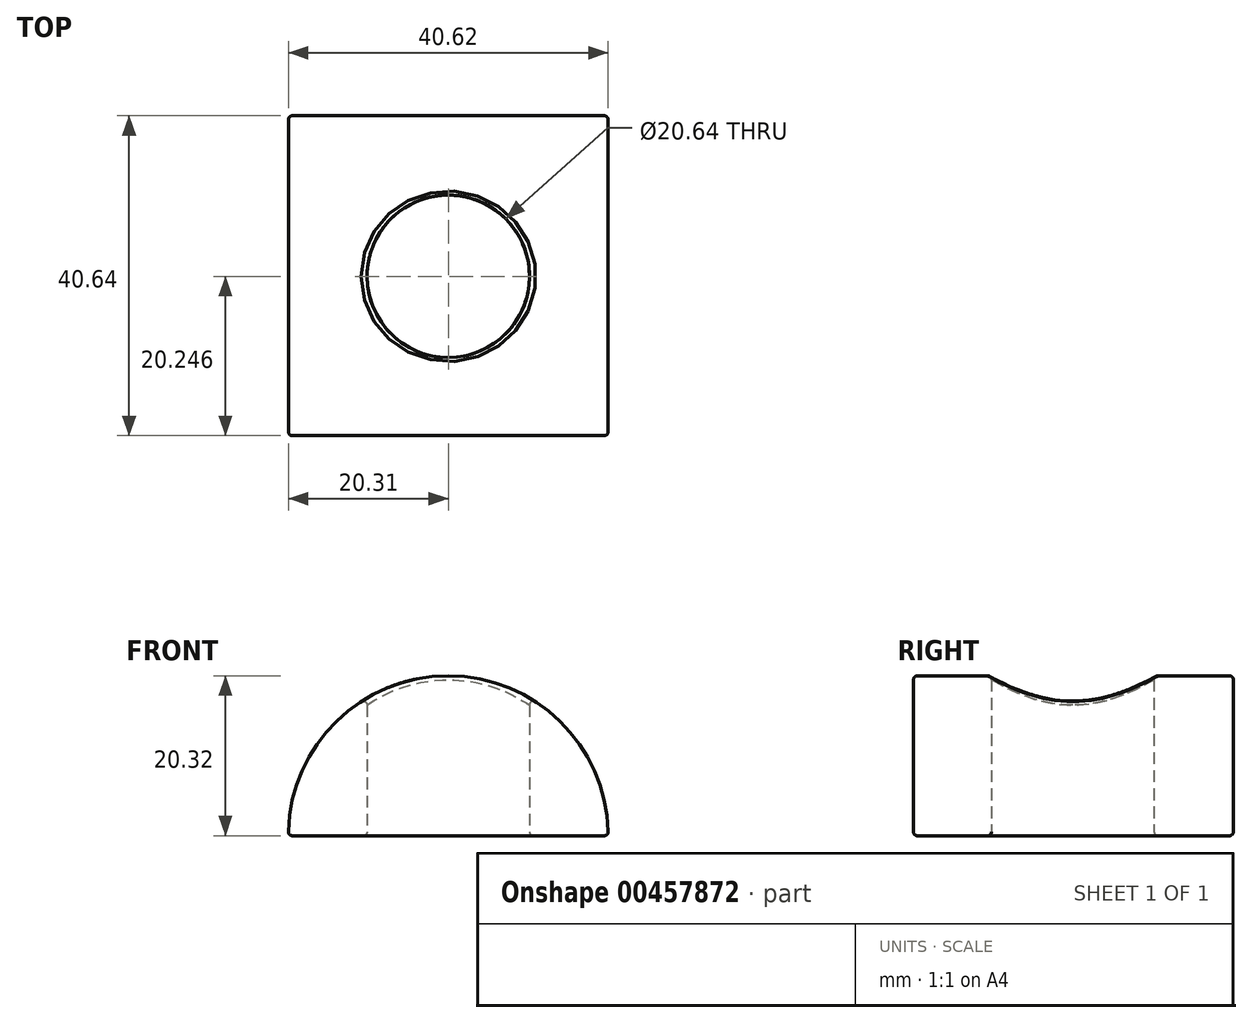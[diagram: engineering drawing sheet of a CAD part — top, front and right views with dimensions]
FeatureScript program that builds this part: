
annotation { "Feature Type Name" : "Feature", "Feature Type Description" : "" }
export const myFeature = defineFeature(function(context is Context, id is Id, definition is map)
    precondition{}
    {
        {
            var Q0;
            Q0=qCreatedBy(makeId("Front.planeOp"),FACE);
            var sketch = newSketch(context, id + "F0", { "sketchPlane" : qUnion([Q0])});
            skLineSegment(sketch, "E0", {"start": v(-20.32, 0) * mm, "end": v(-20.32, 0) * mm});
            skLineSegment(sketch, "E1", {"start": v(20.32, 0) * mm, "end": v(20.32, 0) * mm});
            skLineSegment(sketch, "E2", {"start": v(-20.32, 0) * mm, "end": v(0, 0) * mm, "construction": true});
            skArc(sketch, "E3", {"start": v(20.32, 0) * mm, "mid": v(0, 20.32) * mm, "end": v(-20.32, 0) * mm});
            skLineSegment(sketch, "E4", {"start": v(0, 0) * mm, "end": v(20.32, 0) * mm, "construction": true});
            skLineSegment(sketch, "E5", {"start": v(-20.32, 0) * mm, "end": v(20.32, 0) * mm});
            skSolve(sketch);
        }
        {
            var Q0;
            Q0 = qSketchRegion(id + "F0", true);
            extrude(context, id + "F1", {"entities" : qUnion([Q0]), "depth" : 40.64 * mm});
        }
        {
            var Q0;
            Q0=qCreatedBy(makeId("Top.planeOp"),FACE);
            var sketch = newSketch(context, id + "F2", { "sketchPlane" : qUnion([Q0])});
            skLineSegment(sketch, "E6", {"start": v(0, 0) * mm, "end": v(0, -40.79) * mm, "construction": true});
            skCircle(sketch, "E7", {"center": v(0, -20.4) * mm, "radius": 10.32 * mm});
            skSolve(sketch);
        }
        {
            var Q0;
            Q0 = qSketchRegion(id + "F2", true);
            extrude(context, id + "F3", {"entities" : qUnion([Q0]), "operationType" : NewBodyOperationType.REMOVE, "endBound" : BoundingType.THROUGH_ALL, "depth" : 25.4 * mm});
        }
        {
            var Q0;
            Q0=makeQuery(id+"F1.opExtrude","CAP_FACE",FACE,{"disambiguationData":[OSD([sQuery(id+"F0.wireOp",EDGE,"E3"),sQuery(id+"F0.wireOp",EDGE,"E5")])],"isStart":true});
            var Q1;
            Q1=makeQuery(id+"F1.opExtrude","SWEPT_FACE",FACE,{"disambiguationData":[OSD([sQuery(id+"F0.wireOp",EDGE,"E5")])]});
            var Q2;
            Q2=makeQuery(id+"F1.opExtrude","SWEPT_FACE",FACE,{"disambiguationData":[OSD([sQuery(id+"F0.wireOp",EDGE,"E3")])]});
            fillet(context, id + "F4", {"entities" : qUnion([Q0, Q1, Q2]), "radius" : 0.5 * mm, "tangentPropagation" : true, "allowEdgeOverflow" : false});
        }
    });
